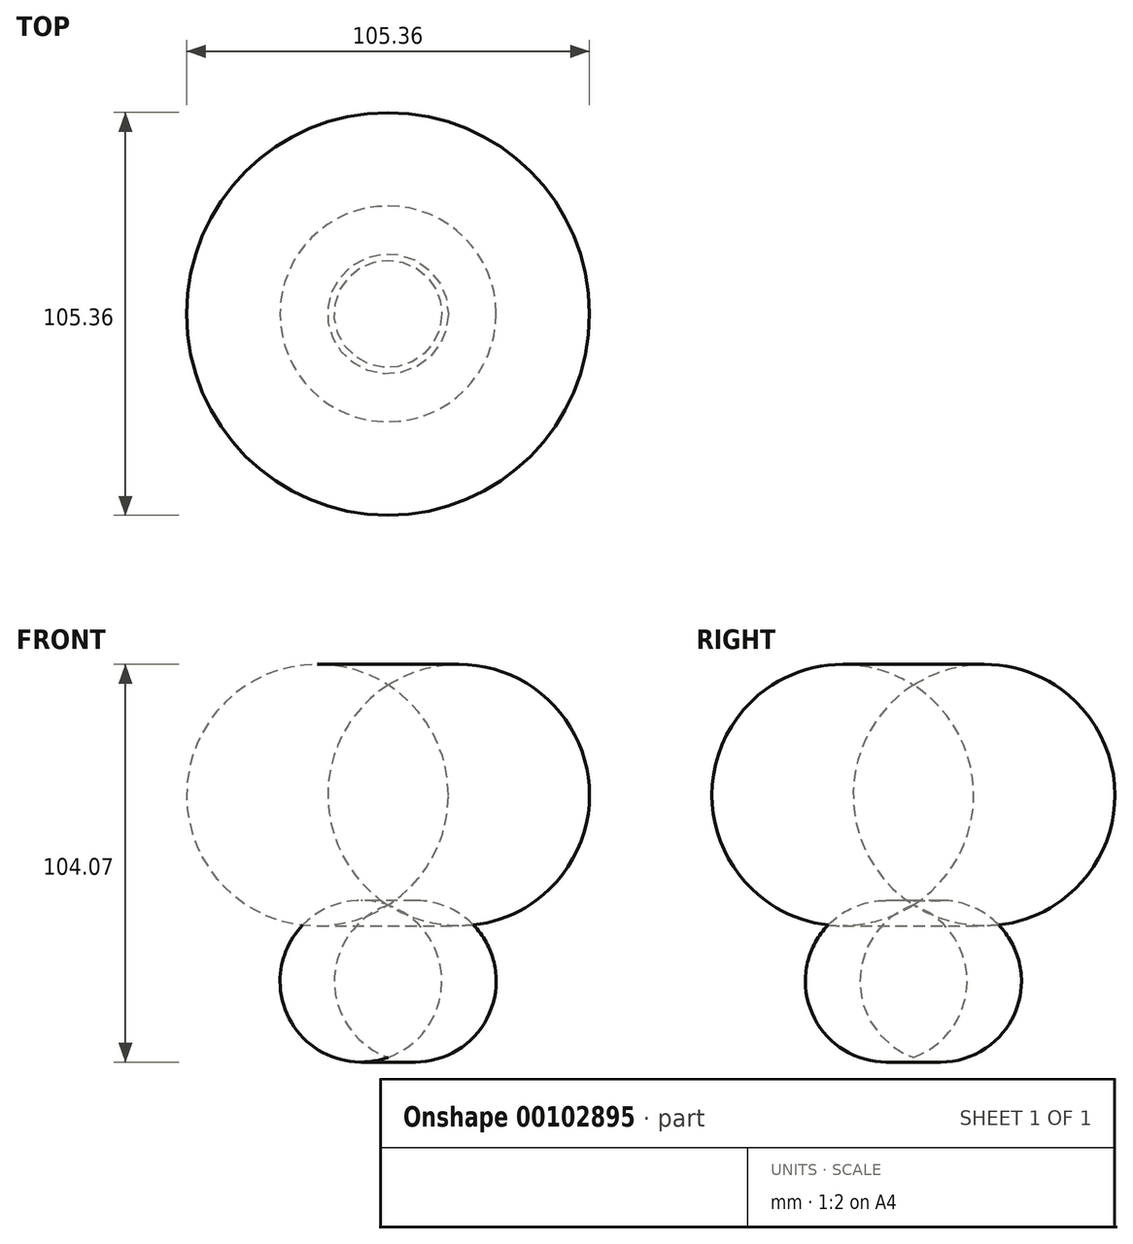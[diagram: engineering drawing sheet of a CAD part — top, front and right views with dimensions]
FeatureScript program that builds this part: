
annotation { "Feature Type Name" : "Feature", "Feature Type Description" : "" }
export const myFeature = defineFeature(function(context is Context, id is Id, definition is map)
    precondition{}
    {
        {
            var Q0;
            Q0=qCreatedBy(makeId("Front.planeOp"),FACE);
            var sketch = newSketch(context, id + "F0", { "sketchPlane" : qUnion([Q0])});
            skLineSegment(sketch, "E0", {"start": v(0, -110.43) * mm, "end": v(0, 119.1) * mm});
            skArc(sketch, "E1", {"start": v(0, -24.68) * mm, "mid": v(15.74, 4.11) * mm, "end": v(0, 32.91) * mm});
            skArc(sketch, "E2", {"start": v(0, -24.68) * mm, "mid": v(-14.05, -44.6) * mm, "end": v(0, -64.53) * mm});
            skSolve(sketch);
        }
        {
            var Q0;
            {var subQ0=sQuery(id+"F0.wireOp",EDGE,"E1");Q0=makeQuery(id+"F0.imprint","IMPRINT",FACE,{"disambiguationData":[TD([[makeQuery(id+"F0.imprint","IMPRINT",EDGE,{"derivedFrom":subQ0}),1.0]])]});}
            var Q1;
            {var subQ0=sQuery(id+"F0.wireOp",EDGE,"E2");Q1=makeQuery(id+"F0.imprint","IMPRINT",FACE,{"disambiguationData":[TD([[makeQuery(id+"F0.imprint","IMPRINT",EDGE,{"derivedFrom":subQ0}),1.0]])]});}
            var Q2;
            Q2=sQuery(id+"F0.wireOp",EDGE,"E0");
            revolve(context, id + "F1", {"entities" : qUnion([Q0, Q1]), "axis" : qUnion([Q2]), "revolveType" : RevolveType.FULL});
        }
    });
